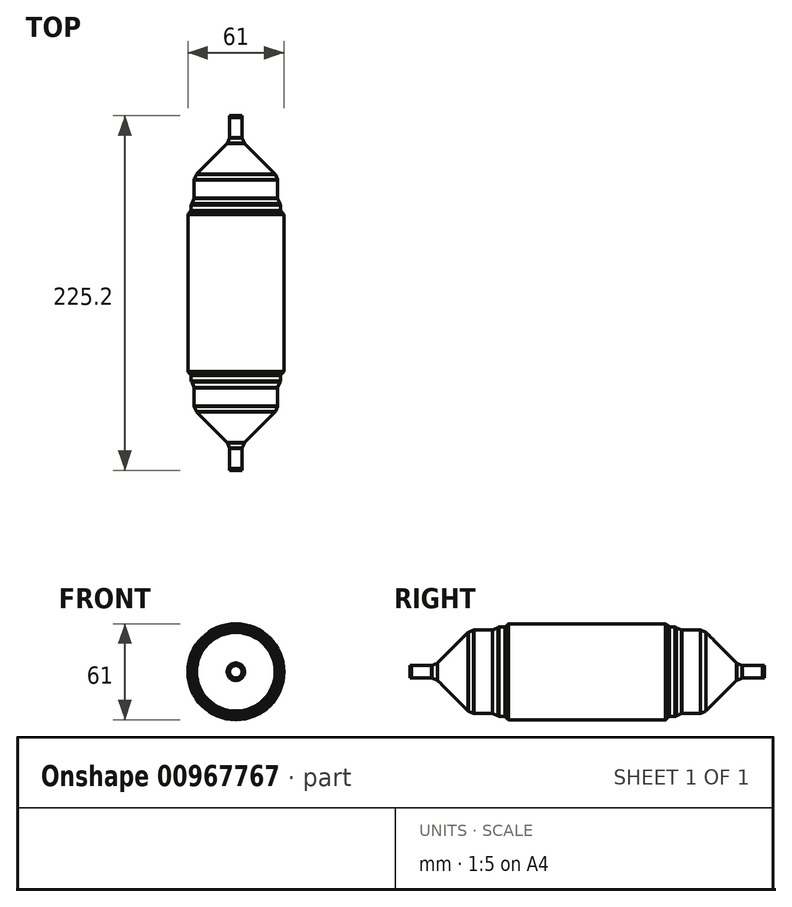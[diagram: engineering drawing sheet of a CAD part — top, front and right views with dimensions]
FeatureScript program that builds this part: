
annotation { "Feature Type Name" : "Feature", "Feature Type Description" : "" }
export const myFeature = defineFeature(function(context is Context, id is Id, definition is map)
    precondition{}
    {
        {
            var Q0;
            Q0=qCreatedBy(makeId("Front.planeOp"),FACE);
            var sketch = newSketch(context, id + "F0", { "sketchPlane" : qUnion([Q0])});
            skCircle(sketch, "E0", {"center": v(0, 0) * mm, "radius": 30.5 * mm});
            skCircle(sketch, "E1", {"center": v(0, 0) * mm, "radius": 28.5 * mm});
            skCircle(sketch, "E2", {"center": v(0, 0) * mm, "radius": 26.5 * mm});
            skCircle(sketch, "E3", {"center": v(0, 0) * mm, "radius": 4 * mm});
            skCircle(sketch, "E4", {"center": v(0, 0) * mm, "radius": 3.95 * mm});
            skSolve(sketch);
        }
        {
            var Q0;
            Q0=makeQuery(id+"F0.imprint","IMPRINT",FACE,{"disambiguationData":[TD([[makeQuery(id+"F0.imprint","IMPRINT",EDGE,{"derivedFrom":sQuery(id+"F0.wireOp",EDGE,"E0")}),1.0]])]});
            extrude(context, id + "F1", {"entities" : qUnion([Q0]), "endBound" : BoundingType.SYMMETRIC, "depth" : 110.1 * mm, "offsetDistance" : 25 * mm});
        }
        {
            var Q0;
            Q0=makeQuery(id+"F0.imprint","IMPRINT",FACE,{"disambiguationData":[TD([[makeQuery(id+"F0.imprint","IMPRINT",EDGE,{"derivedFrom":sQuery(id+"F0.wireOp",EDGE,"E1")}),1.0]])]});
            extrude(context, id + "F2", {"entities" : qUnion([Q0]), "operationType" : NewBodyOperationType.ADD, "endBound" : BoundingType.SYMMETRIC, "depth" : 116.1 * mm, "offsetDistance" : 25 * mm});
        }
        {
            var Q0;
            Q0=makeQuery(id+"F0.imprint","IMPRINT",FACE,{"disambiguationData":[TD([[makeQuery(id+"F0.imprint","IMPRINT",EDGE,{"derivedFrom":sQuery(id+"F0.wireOp",EDGE,"E2")}),1.0]])]});
            extrude(context, id + "F3", {"entities" : qUnion([Q0]), "operationType" : NewBodyOperationType.ADD, "endBound" : BoundingType.SYMMETRIC, "depth" : 200 * mm, "offsetDistance" : 25 * mm});
        }
        {
            var Q0;
            Q0=makeQuery(id+"F0.imprint","IMPRINT",FACE,{"disambiguationData":[TD([[makeQuery(id+"F0.imprint","IMPRINT",EDGE,{"derivedFrom":sQuery(id+"F0.wireOp",EDGE,"E3")}),1.0]])]});
            extrude(context, id + "F4", {"entities" : qUnion([Q0]), "operationType" : NewBodyOperationType.ADD, "endBound" : BoundingType.SYMMETRIC, "depth" : 225 * mm, "offsetDistance" : 25 * mm});
        }
        {
            var Q0;
            Q0=makeQuery(id+"F0.imprint","IMPRINT",FACE,{"disambiguationData":[TD([[makeQuery(id+"F0.imprint","IMPRINT",EDGE,{"derivedFrom":sQuery(id+"F0.wireOp",EDGE,"E4")}),1.0]])]});
            extrude(context, id + "F5", {"entities" : qUnion([Q0]), "operationType" : NewBodyOperationType.ADD, "endBound" : BoundingType.SYMMETRIC, "depth" : 225.2 * mm, "offsetDistance" : 25 * mm});
        }
        {
            var Q0;
            Q0=makeQuery(id+"F2.opExtrude","CAP_EDGE",EDGE,{"disambiguationData":[OSD([sQuery(id+"F0.wireOp",EDGE,"E1")])],"isStart":true});
            var Q1;
            Q1=makeQuery(id+"F2.opExtrude","CAP_EDGE",EDGE,{"disambiguationData":[OSD([sQuery(id+"F0.wireOp",EDGE,"E1")])],"isStart":false});
            chamfer(context, id + "F6", {"entities" : qUnion([Q0, Q1]), "width" : 2 * mm, "tangentPropagation" : true});
        }
        {
            var Q0;
            Q0=makeQuery(id+"F3.opExtrude","CAP_EDGE",EDGE,{"disambiguationData":[OSD([sQuery(id+"F0.wireOp",EDGE,"E2")])],"isStart":true});
            var Q1;
            Q1=makeQuery(id+"F3.opExtrude","CAP_EDGE",EDGE,{"disambiguationData":[OSD([sQuery(id+"F0.wireOp",EDGE,"E2")])],"isStart":false});
            chamfer(context, id + "F7", {"entities" : qUnion([Q0, Q1]), "width" : 26 * mm, "tangentPropagation" : true});
        }
        {
            var Q0;
            Q0=makeQuery(id+"F4.opExtrude","CAP_EDGE",EDGE,{"disambiguationData":[OSD([sQuery(id+"F0.wireOp",EDGE,"E3")])],"isStart":true});
            var Q1;
            Q1=makeQuery(id+"F4.opExtrude","CAP_EDGE",EDGE,{"disambiguationData":[OSD([sQuery(id+"F0.wireOp",EDGE,"E3")])],"isStart":false});
            chamfer(context, id + "F8", {"entities" : qUnion([Q0, Q1]), "width" : 1 * mm, "tangentPropagation" : true});
        }
        {
            var Q0;
            {var subQ0=sQuery(id+"F0.wireOp",EDGE,"E2");Q0=makeQuery(id+"F7.opChamfer","BLEND_FACE",FACE,{"disambiguationData":[OSD([subQ0]),TDD([makeQuery(id+"F3.opExtrude","CAP_EDGE",EDGE,{"disambiguationData":[OSD([subQ0])],"isStart":false})])]});}
            var Q1;
            {var subQ0=sQuery(id+"F0.wireOp",EDGE,"E2");Q1=makeQuery(id+"F3.boolean.opBoolean","SPLIT",FACE,{"disambiguationData":[TD([makeQuery(id+"F2.opExtrude","CAP_FACE",FACE,{"disambiguationData":[OSD([sQuery(id+"F0.wireOp",EDGE,"E1"),subQ0])],"isStart":false})])],"derivedFrom":makeQuery(id+"F3.opExtrude","SWEPT_FACE",FACE,{"disambiguationData":[OSD([subQ0])]})});}
            var Q2;
            Q2=makeQuery(id+"F1.opExtrude","SWEPT_FACE",FACE,{"disambiguationData":[OSD([sQuery(id+"F0.wireOp",EDGE,"E0")])]});
            var Q3;
            {var subQ0=sQuery(id+"F0.wireOp",EDGE,"E2");Q3=makeQuery(id+"F3.boolean.opBoolean","SPLIT",FACE,{"disambiguationData":[TD([makeQuery(id+"F2.opExtrude","CAP_FACE",FACE,{"disambiguationData":[OSD([sQuery(id+"F0.wireOp",EDGE,"E1"),subQ0])],"isStart":true})])],"derivedFrom":makeQuery(id+"F3.opExtrude","SWEPT_FACE",FACE,{"disambiguationData":[OSD([subQ0])]})});}
            var Q4;
            {var subQ0=sQuery(id+"F0.wireOp",EDGE,"E2");Q4=makeQuery(id+"F7.opChamfer","BLEND_FACE",FACE,{"disambiguationData":[OSD([subQ0]),TDD([makeQuery(id+"F3.opExtrude","CAP_EDGE",EDGE,{"disambiguationData":[OSD([subQ0])],"isStart":true})])]});}
            chamfer(context, id + "F9", {"entities" : qUnion([Q0, Q1, Q2, Q3, Q4]), "width" : 5 * mm, "tangentPropagation" : true});
        }
        {
            var Q0;
            {var subQ0=sQuery(id+"F0.wireOp",EDGE,"E3");var subQ1=sQuery(id+"F0.wireOp",EDGE,"E2");Q0=makeQuery(id+"F9.opChamfer","BLEND_FACE",FACE,{"disambiguationData":[OSD([subQ1,subQ0]),TDD([makeQuery(id+"F7.opChamfer","BLEND_EDGE",EDGE,{"blendedFrom":[makeQuery(id+"F3.opExtrude","CAP_EDGE",EDGE,{"disambiguationData":[OSD([subQ1])],"isStart":true}),makeQuery(id+"F4.boolean.opBoolean","SPLIT",FACE,{"disambiguationData":[TD([makeQuery(id+"F3.opExtrude","CAP_FACE",FACE,{"disambiguationData":[OSD([subQ1,subQ0])],"isStart":true})])],"derivedFrom":makeQuery(id+"F4.opExtrude","SWEPT_FACE",FACE,{"disambiguationData":[OSD([subQ0])]})})],"blendedInto":[makeQuery(id+"F4.boolean.opBoolean","SPLIT",FACE,{"disambiguationData":[TD([makeQuery(id+"F3.opExtrude","CAP_FACE",FACE,{"disambiguationData":[OSD([subQ1,subQ0])],"isStart":true})])],"derivedFrom":makeQuery(id+"F4.opExtrude","SWEPT_FACE",FACE,{"disambiguationData":[OSD([subQ0])]})})]})])]});}
            var Q1;
            {var subQ0=sQuery(id+"F0.wireOp",EDGE,"E2");Q1=makeQuery(id+"F7.opChamfer","BLEND_FACE",FACE,{"disambiguationData":[OSD([subQ0]),TDD([makeQuery(id+"F3.opExtrude","CAP_EDGE",EDGE,{"disambiguationData":[OSD([subQ0])],"isStart":true})])]});}
            var Q2;
            {var subQ0=sQuery(id+"F0.wireOp",EDGE,"E2");Q2=makeQuery(id+"F9.opChamfer","BLEND_FACE",FACE,{"disambiguationData":[OSD([subQ0]),TDD([makeQuery(id+"F7.opChamfer","BLEND_EDGE",EDGE,{"blendedFrom":[makeQuery(id+"F3.opExtrude","CAP_EDGE",EDGE,{"disambiguationData":[OSD([subQ0])],"isStart":true}),makeQuery(id+"F3.boolean.opBoolean","SPLIT",FACE,{"disambiguationData":[TD([makeQuery(id+"F2.opExtrude","CAP_FACE",FACE,{"disambiguationData":[OSD([sQuery(id+"F0.wireOp",EDGE,"E1"),subQ0])],"isStart":true})])],"derivedFrom":makeQuery(id+"F3.opExtrude","SWEPT_FACE",FACE,{"disambiguationData":[OSD([subQ0])]})})],"blendedInto":[makeQuery(id+"F3.boolean.opBoolean","SPLIT",FACE,{"disambiguationData":[TD([makeQuery(id+"F2.opExtrude","CAP_FACE",FACE,{"disambiguationData":[OSD([sQuery(id+"F0.wireOp",EDGE,"E1"),subQ0])],"isStart":true})])],"derivedFrom":makeQuery(id+"F3.opExtrude","SWEPT_FACE",FACE,{"disambiguationData":[OSD([subQ0])]})})]})])]});}
            var Q3;
            {var subQ0=sQuery(id+"F0.wireOp",EDGE,"E2");Q3=makeQuery(id+"F3.boolean.opBoolean","SPLIT",FACE,{"disambiguationData":[TD([makeQuery(id+"F2.opExtrude","CAP_FACE",FACE,{"disambiguationData":[OSD([sQuery(id+"F0.wireOp",EDGE,"E1"),subQ0])],"isStart":true})])],"derivedFrom":makeQuery(id+"F3.opExtrude","SWEPT_FACE",FACE,{"disambiguationData":[OSD([subQ0])]})});}
            var Q4;
            {var subQ0=sQuery(id+"F0.wireOp",EDGE,"E2");var subQ1=sQuery(id+"F0.wireOp",EDGE,"E1");Q4=makeQuery(id+"F9.opChamfer","BLEND_FACE",FACE,{"disambiguationData":[OSD([subQ1,subQ0]),TDD([makeQuery(id+"F6.opChamfer","BLEND_EDGE",EDGE,{"blendedFrom":[makeQuery(id+"F2.opExtrude","CAP_EDGE",EDGE,{"disambiguationData":[OSD([subQ1])],"isStart":true}),makeQuery(id+"F3.boolean.opBoolean","SPLIT",FACE,{"disambiguationData":[TD([makeQuery(id+"F2.opExtrude","CAP_FACE",FACE,{"disambiguationData":[OSD([subQ1,subQ0])],"isStart":true})])],"derivedFrom":makeQuery(id+"F3.opExtrude","SWEPT_FACE",FACE,{"disambiguationData":[OSD([subQ0])]})})],"blendedInto":[makeQuery(id+"F3.boolean.opBoolean","SPLIT",FACE,{"disambiguationData":[TD([makeQuery(id+"F2.opExtrude","CAP_FACE",FACE,{"disambiguationData":[OSD([subQ1,subQ0])],"isStart":true})])],"derivedFrom":makeQuery(id+"F3.opExtrude","SWEPT_FACE",FACE,{"disambiguationData":[OSD([subQ0])]})})]})])]});}
            var Q5;
            {var subQ0=sQuery(id+"F0.wireOp",EDGE,"E1");Q5=makeQuery(id+"F2.boolean.opBoolean","SPLIT",FACE,{"disambiguationData":[TD([makeQuery(id+"F1.opExtrude","CAP_FACE",FACE,{"disambiguationData":[OSD([sQuery(id+"F0.wireOp",EDGE,"E0"),subQ0])],"isStart":true})])],"derivedFrom":makeQuery(id+"F2.opExtrude","SWEPT_FACE",FACE,{"disambiguationData":[OSD([subQ0])]})});}
            var Q6;
            Q6=makeQuery(id+"F1.opExtrude","SWEPT_FACE",FACE,{"disambiguationData":[OSD([sQuery(id+"F0.wireOp",EDGE,"E0")])]});
            var Q7;
            {var subQ0=sQuery(id+"F0.wireOp",EDGE,"E1");Q7=makeQuery(id+"F2.boolean.opBoolean","SPLIT",FACE,{"disambiguationData":[TD([makeQuery(id+"F1.opExtrude","CAP_FACE",FACE,{"disambiguationData":[OSD([sQuery(id+"F0.wireOp",EDGE,"E0"),subQ0])],"isStart":false})])],"derivedFrom":makeQuery(id+"F2.opExtrude","SWEPT_FACE",FACE,{"disambiguationData":[OSD([subQ0])]})});}
            var Q8;
            {var subQ0=sQuery(id+"F0.wireOp",EDGE,"E2");var subQ1=sQuery(id+"F0.wireOp",EDGE,"E1");var subQ2=makeQuery(id+"F3.boolean.opBoolean","SPLIT",FACE,{"disambiguationData":[TD([makeQuery(id+"F2.opExtrude","CAP_FACE",FACE,{"disambiguationData":[OSD([subQ1,subQ0])],"isStart":false})])],"derivedFrom":makeQuery(id+"F3.opExtrude","SWEPT_FACE",FACE,{"disambiguationData":[OSD([subQ0])]})});Q8=makeQuery(id+"F9.opChamfer","BLEND_EDGE",EDGE,{"blendedFrom":[makeQuery(id+"F6.opChamfer","BLEND_EDGE",EDGE,{"blendedFrom":[makeQuery(id+"F2.opExtrude","CAP_EDGE",EDGE,{"disambiguationData":[OSD([subQ1])],"isStart":false}),subQ2],"blendedInto":[subQ2]}),subQ2],"blendedInto":[subQ2]});}
            var Q9;
            {var subQ0=sQuery(id+"F0.wireOp",EDGE,"E2");Q9=makeQuery(id+"F9.opChamfer","BLEND_FACE",FACE,{"disambiguationData":[OSD([subQ0]),TDD([makeQuery(id+"F7.opChamfer","BLEND_EDGE",EDGE,{"blendedFrom":[makeQuery(id+"F3.opExtrude","CAP_EDGE",EDGE,{"disambiguationData":[OSD([subQ0])],"isStart":false}),makeQuery(id+"F3.boolean.opBoolean","SPLIT",FACE,{"disambiguationData":[TD([makeQuery(id+"F2.opExtrude","CAP_FACE",FACE,{"disambiguationData":[OSD([sQuery(id+"F0.wireOp",EDGE,"E1"),subQ0])],"isStart":false})])],"derivedFrom":makeQuery(id+"F3.opExtrude","SWEPT_FACE",FACE,{"disambiguationData":[OSD([subQ0])]})})],"blendedInto":[makeQuery(id+"F3.boolean.opBoolean","SPLIT",FACE,{"disambiguationData":[TD([makeQuery(id+"F2.opExtrude","CAP_FACE",FACE,{"disambiguationData":[OSD([sQuery(id+"F0.wireOp",EDGE,"E1"),subQ0])],"isStart":false})])],"derivedFrom":makeQuery(id+"F3.opExtrude","SWEPT_FACE",FACE,{"disambiguationData":[OSD([subQ0])]})})]})])]});}
            var Q10;
            {var subQ0=sQuery(id+"F0.wireOp",EDGE,"E2");Q10=makeQuery(id+"F7.opChamfer","BLEND_FACE",FACE,{"disambiguationData":[OSD([subQ0]),TDD([makeQuery(id+"F3.opExtrude","CAP_EDGE",EDGE,{"disambiguationData":[OSD([subQ0])],"isStart":false})])]});}
            var Q11;
            {var subQ0=sQuery(id+"F0.wireOp",EDGE,"E3");var subQ1=sQuery(id+"F0.wireOp",EDGE,"E2");Q11=makeQuery(id+"F9.opChamfer","BLEND_FACE",FACE,{"disambiguationData":[OSD([subQ1,subQ0]),TDD([makeQuery(id+"F7.opChamfer","BLEND_EDGE",EDGE,{"blendedFrom":[makeQuery(id+"F3.opExtrude","CAP_EDGE",EDGE,{"disambiguationData":[OSD([subQ1])],"isStart":false}),makeQuery(id+"F4.boolean.opBoolean","SPLIT",FACE,{"disambiguationData":[TD([makeQuery(id+"F3.opExtrude","CAP_FACE",FACE,{"disambiguationData":[OSD([subQ1,subQ0])],"isStart":false})])],"derivedFrom":makeQuery(id+"F4.opExtrude","SWEPT_FACE",FACE,{"disambiguationData":[OSD([subQ0])]})})],"blendedInto":[makeQuery(id+"F4.boolean.opBoolean","SPLIT",FACE,{"disambiguationData":[TD([makeQuery(id+"F3.opExtrude","CAP_FACE",FACE,{"disambiguationData":[OSD([subQ1,subQ0])],"isStart":false})])],"derivedFrom":makeQuery(id+"F4.opExtrude","SWEPT_FACE",FACE,{"disambiguationData":[OSD([subQ0])]})})]})])]});}
            chamfer(context, id + "F10", {"entities" : qUnion([Q0, Q1, Q2, Q3, Q4, Q5, Q6, Q7, Q8, Q9, Q10, Q11]), "width" : 0.5 * mm, "tangentPropagation" : true});
        }
    });
